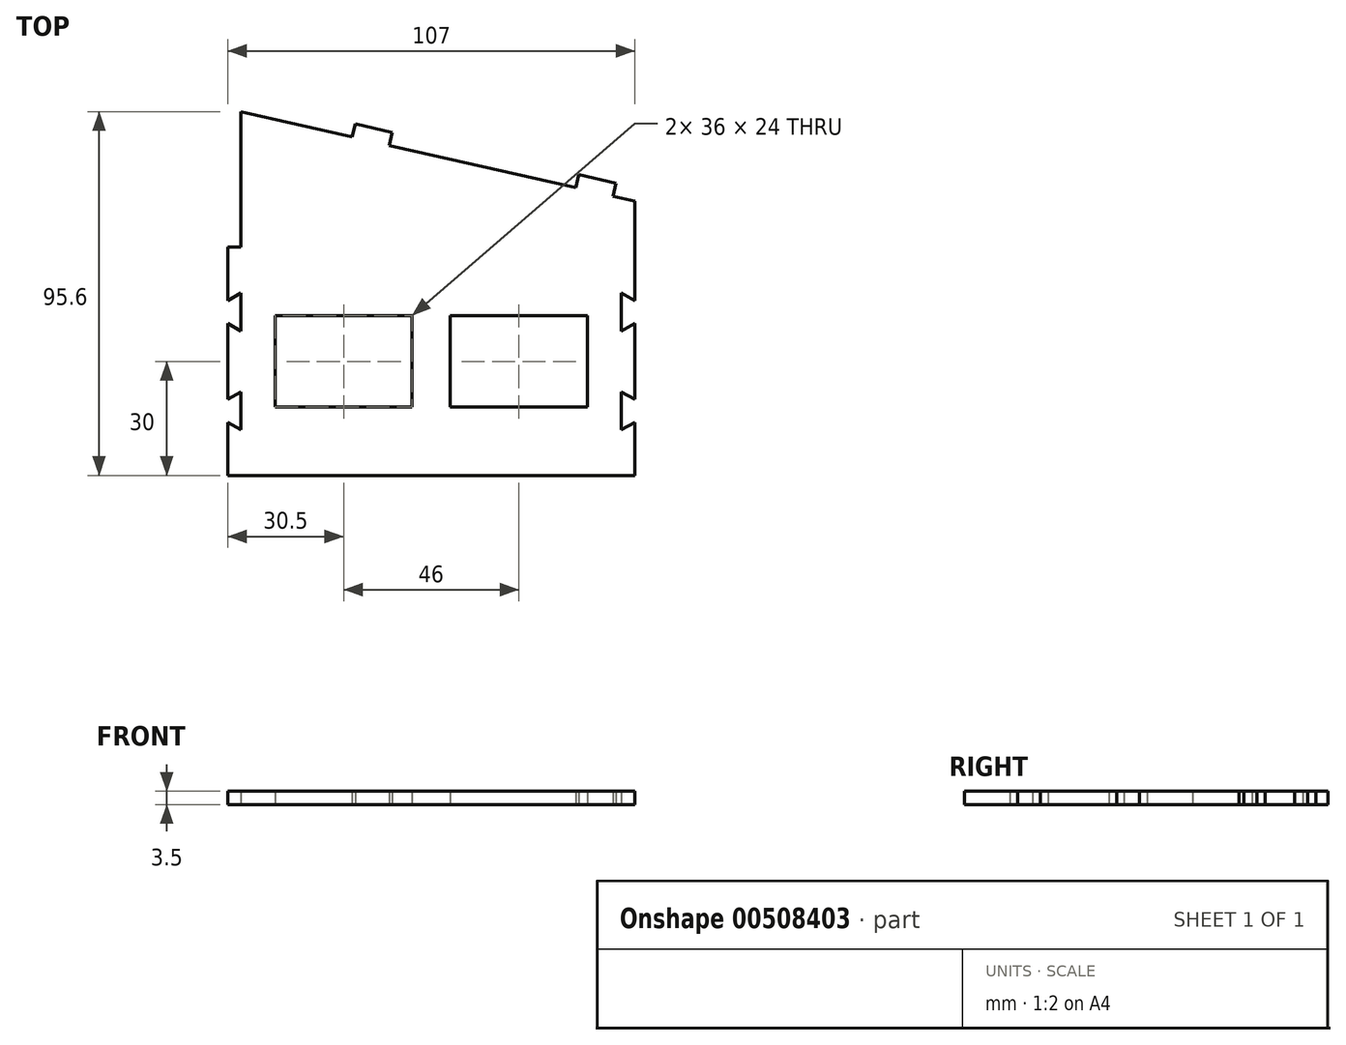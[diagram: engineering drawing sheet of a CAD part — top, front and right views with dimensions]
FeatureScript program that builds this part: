
annotation { "Feature Type Name" : "Feature", "Feature Type Description" : "" }
export const myFeature = defineFeature(function(context is Context, id is Id, definition is map)
    precondition{}
    {
        {
            var Q0;
            Q0=qCreatedBy(makeId("Top.planeOp"),FACE);
            var sketch = newSketch(context, id + "F0", { "sketchPlane" : qUnion([Q0])});
            skLineSegment(sketch, "E0.bottom", {"start": v(53.5, -30) * mm, "end": v(-53.5, -30) * mm});
            skPoint(sketch, "E0.middle", {"position": v(0, 0) * mm});
            skLineSegment(sketch, "E1", {"start": v(-53.5, -30) * mm, "end": v(-50, -30) * mm});
            skLineSegment(sketch, "E2", {"start": v(-50, -30) * mm, "end": v(-41, -30) * mm});
            skLineSegment(sketch, "E3", {"start": v(-41, -12) * mm, "end": v(-5, -12) * mm});
            skLineSegment(sketch, "E4", {"start": v(-5, -12) * mm, "end": v(-5, 12) * mm});
            skLineSegment(sketch, "E5", {"start": v(-5, 12) * mm, "end": v(-41, 12) * mm});
            skLineSegment(sketch, "E6", {"start": v(-41, 12) * mm, "end": v(-41, -12) * mm});
            skLineSegment(sketch, "E7", {"start": v(5, -12) * mm, "end": v(41, -12) * mm});
            skLineSegment(sketch, "E8", {"start": v(41, -12) * mm, "end": v(41, 12) * mm});
            skLineSegment(sketch, "E9", {"start": v(41, 12) * mm, "end": v(5, 12) * mm});
            skLineSegment(sketch, "E10", {"start": v(5, 12) * mm, "end": v(5, -12) * mm});
            skLineSegment(sketch, "E11", {"start": v(-53.5, 30) * mm, "end": v(-53.5, 16) * mm});
            skLineSegment(sketch, "E12", {"start": v(-53.5, 10) * mm, "end": v(-53.5, -10) * mm});
            skLineSegment(sketch, "E13", {"start": v(-53.5, -16) * mm, "end": v(-53.5, -30) * mm});
            skLineSegment(sketch, "E14", {"start": v(-50, 13) * mm, "end": v(-50, 18) * mm});
            skLineSegment(sketch, "E15", {"start": v(-50, 18) * mm, "end": v(-50, 8) * mm});
            skLineSegment(sketch, "E16", {"start": v(-50, 8) * mm, "end": v(-53.5, 10) * mm});
            skLineSegment(sketch, "E17", {"start": v(-50, 18) * mm, "end": v(-53.5, 16) * mm});
            skLineSegment(sketch, "E18", {"start": v(-50, -13) * mm, "end": v(-50, -8) * mm});
            skLineSegment(sketch, "E19", {"start": v(-50, -8) * mm, "end": v(-50, -18) * mm});
            skPoint(sketch, "E19.endSnap0", {"position": v(-50, -10.5) * mm});
            skLineSegment(sketch, "E20", {"start": v(-50, -18) * mm, "end": v(-53.5, -16) * mm});
            skLineSegment(sketch, "E21", {"start": v(-50, -8) * mm, "end": v(-53.5, -10) * mm});
            skLineSegment(sketch, "E22", {"start": v(53.5, 30) * mm, "end": v(53.5, 16) * mm});
            skLineSegment(sketch, "E23", {"start": v(53.5, 10) * mm, "end": v(53.5, -10) * mm});
            skLineSegment(sketch, "E24", {"start": v(53.5, -16) * mm, "end": v(53.5, -30) * mm});
            skLineSegment(sketch, "E25", {"start": v(50, -13) * mm, "end": v(50, -8) * mm});
            skLineSegment(sketch, "E26", {"start": v(50, -8) * mm, "end": v(53.5, -10) * mm});
            skLineSegment(sketch, "E27", {"start": v(50, -13) * mm, "end": v(50, -18) * mm});
            skLineSegment(sketch, "E28", {"start": v(50, -18) * mm, "end": v(53.5, -16) * mm});
            skLineSegment(sketch, "E29", {"start": v(50, 13) * mm, "end": v(50, 18) * mm});
            skLineSegment(sketch, "E30", {"start": v(50, 18) * mm, "end": v(53.5, 16) * mm});
            skLineSegment(sketch, "E31", {"start": v(50, 13) * mm, "end": v(50, 8) * mm});
            skLineSegment(sketch, "E32", {"start": v(50, 8) * mm, "end": v(53.5, 10) * mm});
            skLineSegment(sketch, "E33", {"start": v(-20.74, 58.97) * mm, "end": v(-19.97, 62.38) * mm});
            skLineSegment(sketch, "E34", {"start": v(-19.97, 62.38) * mm, "end": v(-10.22, 60.17) * mm});
            skLineSegment(sketch, "E35", {"start": v(-10.22, 60.17) * mm, "end": v(-11, 56.75) * mm});
            skLineSegment(sketch, "E36", {"start": v(47.74, 43.44) * mm, "end": v(48.52, 46.85) * mm});
            skLineSegment(sketch, "E37", {"start": v(48.52, 46.85) * mm, "end": v(38.76, 49.06) * mm});
            skLineSegment(sketch, "E38", {"start": v(38.76, 49.06) * mm, "end": v(38, 45.65) * mm});
            skLineSegment(sketch, "E39", {"start": v(38, 45.65) * mm, "end": v(-11, 56.75) * mm});
            skLineSegment(sketch, "E40", {"start": v(53.5, 30) * mm, "end": v(53.5, 42.13) * mm});
            skLineSegment(sketch, "E41", {"start": v(53.5, 42.13) * mm, "end": v(47.74, 43.44) * mm});
            skLineSegment(sketch, "E42", {"start": v(-50, 65.6) * mm, "end": v(-50, 30) * mm});
            skLineSegment(sketch, "E43", {"start": v(-50, 30) * mm, "end": v(-53.5, 30) * mm});
            skLineSegment(sketch, "E44", {"start": v(-50, 65.6) * mm, "end": v(-20.74, 58.97) * mm});
            skSolve(sketch);
        }
        {
            var Q0;
            Q0=makeQuery(id+"F0.imprint","IMPRINT",FACE,{"disambiguationData":[TD([[makeQuery(id+"F0.imprint","IMPRINT",EDGE,{"derivedFrom":sQuery(id+"F0.wireOp",EDGE,"E0.bottom")}),-1.0]])]});
            extrude(context, id + "F1", {"entities" : qUnion([Q0]), "depth" : 3.5 * mm, "offsetDistance" : 25 * mm});
        }
    });
